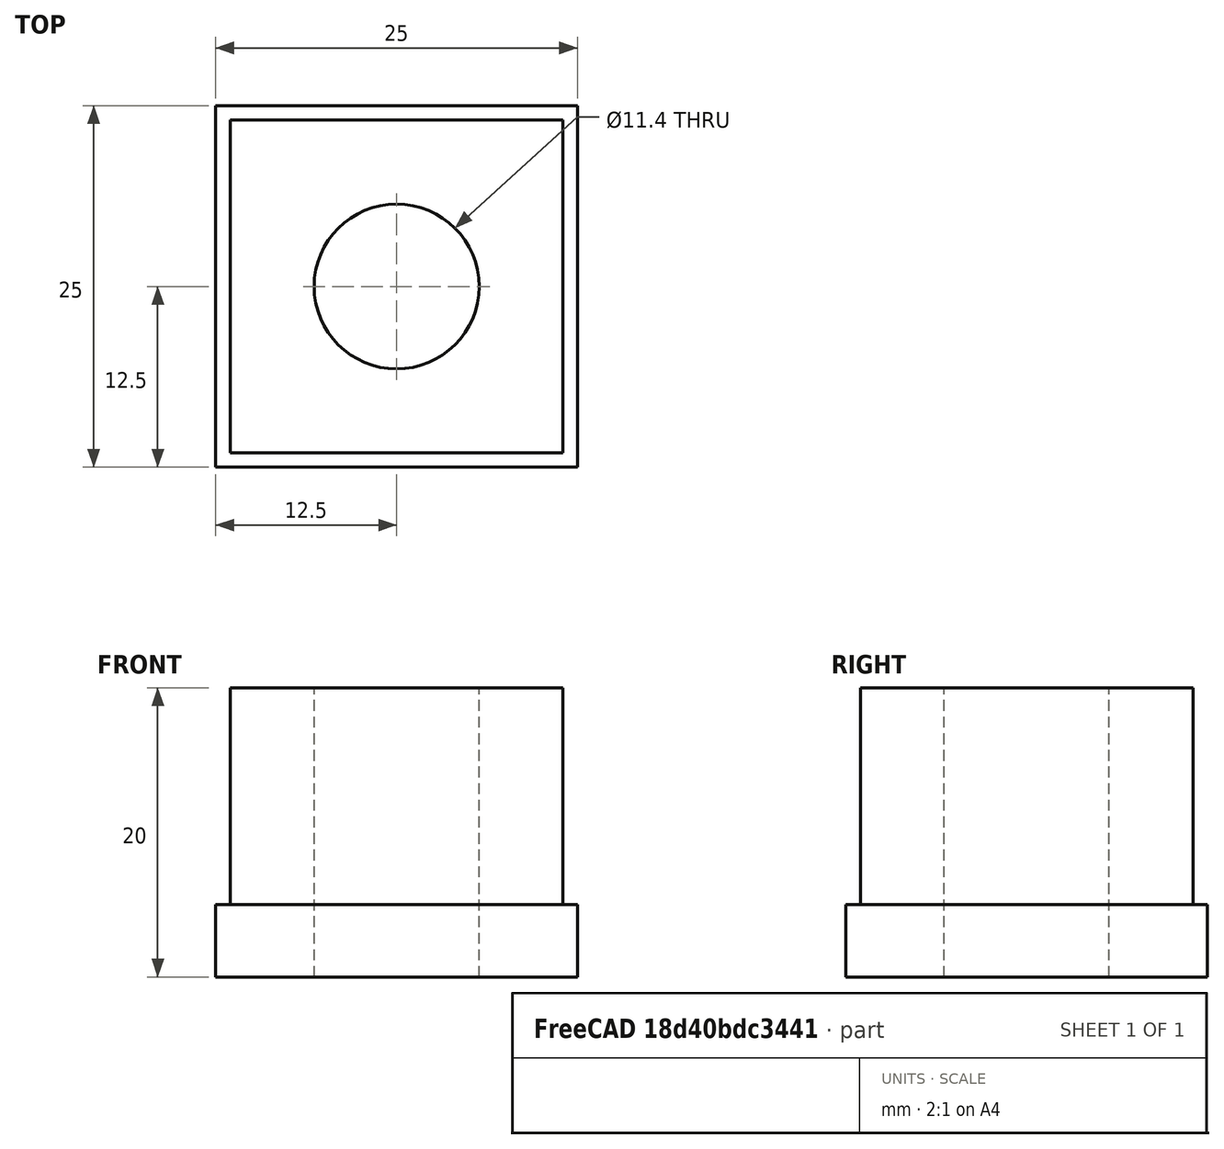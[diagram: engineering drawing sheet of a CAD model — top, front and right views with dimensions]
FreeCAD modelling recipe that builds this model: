
FCSTD DOCUMENT  (FreeCAD 0.19R24276 (Git))
Label: tapaRuedas
License: All rights reserved
LicenseURL: http://en.wikipedia.org/wiki/All_rights_reserved
objects: TechDraw::DrawViewDimension×6, TechDraw::DrawProjGroupItem×3, Part::Box×2, TechDraw::DrawSVGTemplate×2, TechDraw::DrawViewPart×2, TechDraw::DrawPage×2, Part::Cylinder×1, Part::MultiFuse×1, Part::Offset×1, Part::Cut×1, TechDraw::DrawProjGroup×1, TechDraw::DrawViewAnnotation×1
note: 6 computed .brp shape members not serialized (recipe doc carries the construction recipe); baked Part::Feature solids carry a one-line shape summary decoded from their .brp

FEATURE [Part::Box] Box  label="Cubo"
  AttacherType = Attacher::AttachEngine3D
  Height = 5
  Length = 25
  Width = 25
FEATURE [Part::Box] Box001  label="Cubo001"
  AttacherType = Attacher::AttachEngine3D
  Height = 15
  Length = 23
  Placement = pos=(1,1,5) rot=(0,0,1;0rad)
  Width = 23
FEATURE [Part::Cylinder] Cylinder  label="Cilindro"
  Angle = 360
  AttacherType = Attacher::AttachEngine3D
  Height = 20
  Placement = pos=(12.5,12.5,0) rot=(0,0,1;0rad)
  Radius = 5.5
FEATURE [Part::MultiFuse] Fusion
  Shapes = -> [Box001,Box]
FEATURE [Part::Offset] Offset
  Fill = false
  Intersection = false
  Join = 0
  Mode = 0
  SelfIntersection = false
  Source = -> Cylinder
  Value = 0.2
FEATURE [Part::Cut] Cut
  Base = -> Fusion
  Tool = -> Offset
FEATURE [TechDraw::DrawSVGTemplate] Template
  EditableTexts = Designed_by_Name=<owner>; Drawing_number=001; FC-Date=-; FC-SC=2:1; FC-SH=1/2; FC-Title=OfficeChairWheelAdaptor; Subtitle=Adaptador Rueda Oficina; Weight=<100gr
  Height = 210
  Orientation = 1
  Width = 297
FEATURE [TechDraw::DrawSVGTemplate] Template001
  EditableTexts = Designed_by_Name=<owner>; Drawing_number=001; FC-Date=-; FC-SC=3:1; FC-SH=2/2; FC-Title=OfficeChairWheelAdaptor; Subtitle=Adaptador Rueda Oficina; Weight=<100gr
  Height = 210
  Orientation = 1
  Width = 297
FEATURE [TechDraw::DrawViewPart] View
  CoarseView = false
  Direction = (0.577,-0.577,0.577)
  Focus = 100
  HardHidden = false
  IsoCount = 0
  IsoHidden = false
  IsoVisible = false
  LockPosition = false
  Perspective = false
  Rotation = 0
  Scale = 3
  ScaleType = 0
  SeamHidden = false
  SeamVisible = true
  SmoothHidden = false
  SmoothVisible = true
  Source = -> [Cut]
  X = 211.7
  XDirection = (0.707,0.707,0)
  Y = 129.467
FEATURE [TechDraw::DrawViewPart] View001
  CoarseView = false
  Direction = (0.577,-0.577,0.577)
  Focus = 100
  HardHidden = false
  IsoCount = 0
  IsoHidden = false
  IsoVisible = false
  LockPosition = false
  Perspective = false
  Rotation = 0
  Scale = 3
  ScaleType = 0
  SeamHidden = false
  SeamVisible = true
  SmoothHidden = false
  SmoothVisible = true
  Source = -> [Cut]
  X = 152.5
  XDirection = (0.707,0.707,0)
  Y = 130.2
FEATURE [TechDraw::DrawProjGroupItem] ProjItem  label="Front"
  CoarseView = false
  Direction = (0,-1,0)
  Focus = 100
  HardHidden = false
  IsoCount = 0
  IsoHidden = false
  IsoVisible = false
  LockPosition = true
  Perspective = false
  Rotation = 0
  RotationVector = (1,0,0)
  Scale = 2
  ScaleType = 2
  SeamHidden = false
  SeamVisible = true
  SmoothHidden = false
  SmoothVisible = true
  Source = -> [Cut]
  Type = 0
  X = 0
  XDirection = (1,0,0)
  Y = 0
FEATURE [TechDraw::DrawProjGroupItem] ProjItem001  label="Right"
  CoarseView = false
  Direction = (1,-1e-16,0)
  Focus = 100
  HardHidden = false
  IsoCount = 0
  IsoHidden = false
  IsoVisible = false
  LockPosition = false
  Perspective = false
  Rotation = 0
  RotationVector = (1,0,0)
  ScaleType = 2
  SeamHidden = false
  SeamVisible = true
  SmoothHidden = false
  SmoothVisible = true
  Source = -> [Cut]
  Type = 2
  X = -65
  XDirection = (1e-16,1,0)
  Y = 0
FEATURE [TechDraw::DrawProjGroupItem] ProjItem002  label="Top"
  CoarseView = false
  Direction = (0,0,1)
  Focus = 100
  HardHidden = false
  IsoCount = 0
  IsoHidden = false
  IsoVisible = false
  LockPosition = false
  Perspective = false
  Rotation = 0
  RotationVector = (1,0,0)
  ScaleType = 2
  SeamHidden = false
  SeamVisible = true
  SmoothHidden = false
  SmoothVisible = true
  Source = -> [Cut]
  Type = 4
  X = 0
  XDirection = (1,0,0)
  Y = -65
FEATURE [TechDraw::DrawProjGroup] ProjGroup
  Anchor = -> ProjItem
  AutoDistribute = true
  LockPosition = false
  ProjectionType = 0
  Rotation = 0
  Scale = 2
  ScaleType = 2
  Source = -> [Cut]
  Views = -> [ProjItem,ProjItem001,ProjItem002]
  X = 114.5
  Y = 163.8
  spacingX = 15
  spacingY = 15
FEATURE [TechDraw::DrawViewDimension] Dimension
  Arbitrary = false
  ArbitraryTolerances = false
  EqualTolerance = true
  FormatSpec = %.2f
  FormatSpecOverTolerance = %+.2f
  FormatSpecUnderTolerance = %+.2f
  Inverted = false
  LockPosition = false
  MeasureType = 1
  OverTolerance = 0
  References2D = -> [ProjItem]
  Rotation = 0
  ScaleType = 0
  TheoreticalExact = false
  Type = 1
  UnderTolerance = 0
  X = -0.666667
  Y = -23
FEATURE [TechDraw::DrawViewDimension] Dimension001
  Arbitrary = false
  ArbitraryTolerances = false
  EqualTolerance = true
  FormatSpec = %.2f
  FormatSpecOverTolerance = %+.2f
  FormatSpecUnderTolerance = %+.2f
  Inverted = false
  LockPosition = false
  MeasureType = 1
  OverTolerance = 0
  References2D = -> [ProjItem]
  Rotation = 0
  ScaleType = 0
  TheoreticalExact = false
  Type = 2
  UnderTolerance = 0
  X = 24
  Y = 0
FEATURE [TechDraw::DrawViewDimension] Dimension002
  Arbitrary = false
  ArbitraryTolerances = false
  EqualTolerance = true
  FormatSpec = ⌀%.2f
  FormatSpecOverTolerance = %+.2f
  FormatSpecUnderTolerance = %+.2f
  Inverted = false
  LockPosition = false
  MeasureType = 1
  OverTolerance = 0
  References2D = -> [ProjItem002]
  Rotation = 0
  ScaleType = 0
  TheoreticalExact = false
  Type = 5
  UnderTolerance = 0
  X = -46
  Y = 6.33333
FEATURE [TechDraw::DrawPage] Page  label="Vistas"
  KeepUpdated = true
  NextBalloonIndex = 1
  ProjectionType = 0
  Template = -> Template
  Views = -> [View,ProjGroup,Dimension,Dimension001,Dimension002]
FEATURE [TechDraw::DrawViewDimension] Dimension003
  Arbitrary = false
  ArbitraryTolerances = false
  EqualTolerance = true
  FormatSpec = %.2f
  FormatSpecOverTolerance = %+.2f
  FormatSpecUnderTolerance = %+.2f
  Inverted = false
  LockPosition = false
  MeasureType = 1
  OverTolerance = 0
  References2D = -> [View001]
  Rotation = 0
  ScaleType = 0
  TheoreticalExact = false
  Type = 0
  UnderTolerance = 0
  X = 26.8454
  Y = -48.7296
FEATURE [TechDraw::DrawViewDimension] Dimension004
  Arbitrary = false
  ArbitraryTolerances = false
  EqualTolerance = true
  FormatSpec = %.2f
  FormatSpecOverTolerance = %+.2f
  FormatSpecUnderTolerance = %+.2f
  Inverted = false
  LockPosition = false
  MeasureType = 1
  OverTolerance = 0
  References2D = -> [View001]
  Rotation = 0
  ScaleType = 0
  TheoreticalExact = false
  Type = 0
  UnderTolerance = 0
  X = -77.4356
  Y = -2.40606
FEATURE [TechDraw::DrawViewDimension] Dimension005
  Arbitrary = false
  ArbitraryTolerances = false
  EqualTolerance = true
  FormatSpec = %.2f
  FormatSpecOverTolerance = %+.2f
  FormatSpecUnderTolerance = %+.2f
  Inverted = false
  LockPosition = false
  MeasureType = 1
  OverTolerance = 0
  References2D = -> [View001]
  Rotation = 0
  ScaleType = 0
  TheoreticalExact = false
  Type = 2
  UnderTolerance = 0
  X = 57.3105
  Y = 8.72792
FEATURE [TechDraw::DrawViewAnnotation] Annotation
  Font = osifont
  LineSpace = 80
  LockPosition = false
  MaxWidth = -1
  Rotation = 0
  ScaleType = 0
  Text = Aproximate measurements: | Check with 3D piece
  TextSize = 5
  TextStyle = 0
  X = 68.5
  Y = 75.4
FEATURE [TechDraw::DrawPage] Page001  label="Cotas"
  KeepUpdated = true
  NextBalloonIndex = 1
  ProjectionType = 0
  Template = -> Template001
  Views = -> [View001,Dimension003,Dimension004,Dimension005,Annotation]
